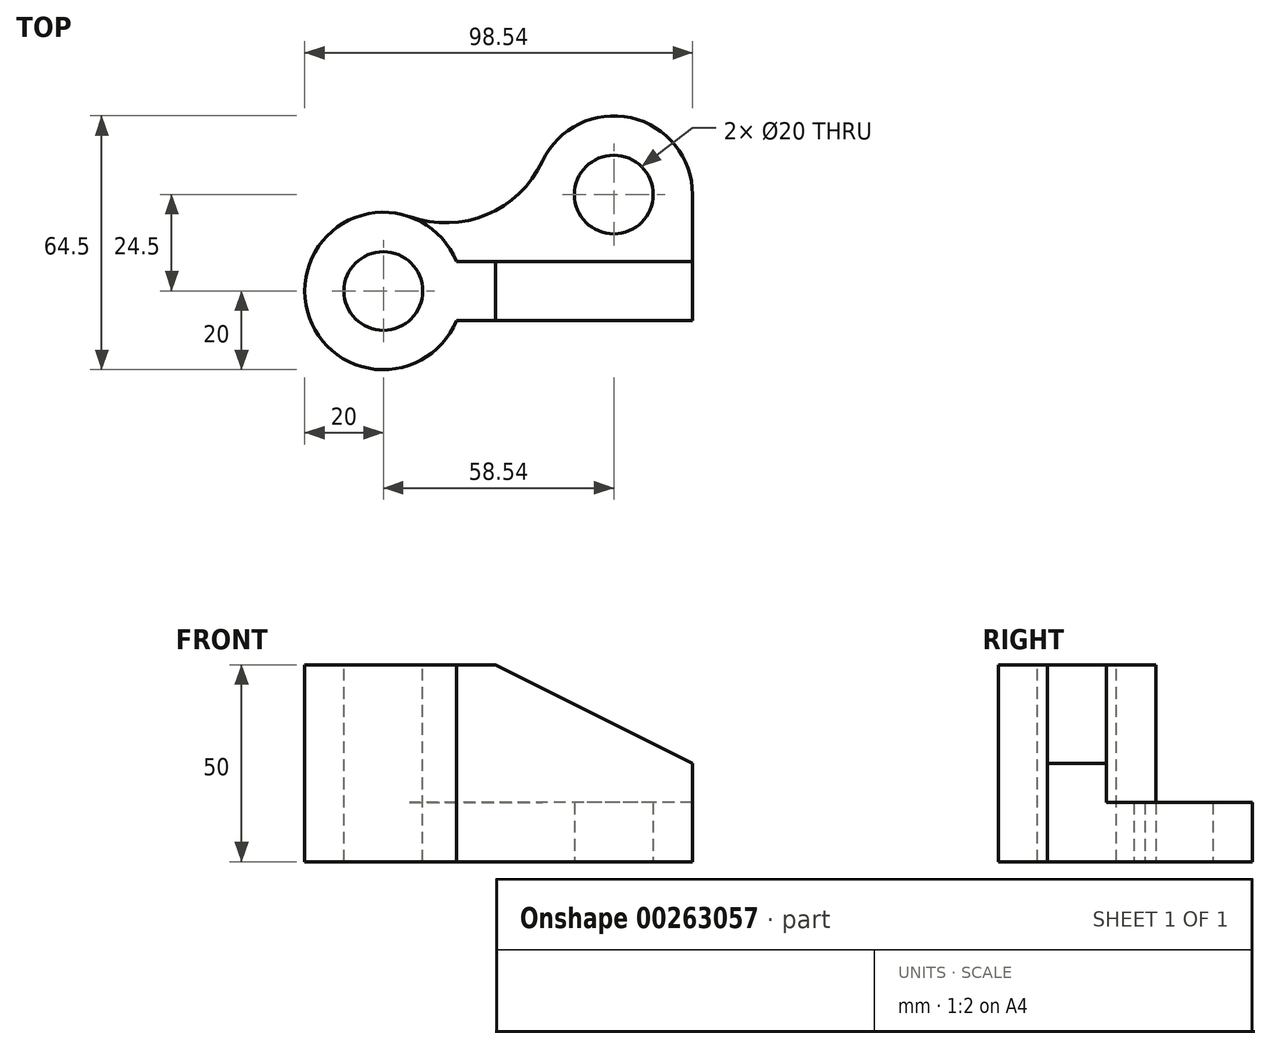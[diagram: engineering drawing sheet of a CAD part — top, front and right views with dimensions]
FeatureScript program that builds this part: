
annotation { "Feature Type Name" : "Feature", "Feature Type Description" : "" }
export const myFeature = defineFeature(function(context is Context, id is Id, definition is map)
    precondition{}
    {
        {
            var Q0;
            Q0=qCreatedBy(makeId("Top.planeOp"),FACE);
            var sketch = newSketch(context, id + "F0", { "sketchPlane" : qUnion([Q0])});
            skLineSegment(sketch, "E0", {"start": v(0, 0) * mm, "end": v(0, 32) * mm});
            skPoint(sketch, "E1", {"position": v(-78.54, 7.5) * mm});
            skLineSegment(sketch, "E2", {"start": v(0, 0) * mm, "end": v(-60, 0) * mm});
            skArc(sketch, "E3", {"start": v(0, 32) * mm, "mid": v(-15.65, 51.52) * mm, "end": v(-38.1, 40.5) * mm});
            skArc(sketch, "E4", {"start": v(-71.89, 26.36) * mm, "mid": v(-96.77, -0.72) * mm, "end": v(-60, 0) * mm});
            skArc(sketch, "E5", {"start": v(-71.89, 26.36) * mm, "mid": v(-52.27, 26.92) * mm, "end": v(-38.1, 40.5) * mm});
            skCircle(sketch, "E6", {"center": v(-20, 32) * mm, "radius": 10 * mm});
            skSolve(sketch);
        }
        {
            var Q0;
            Q0 = qSketchRegion(id + "F0", true);
            extrude(context, id + "F1", {"entities" : qUnion([Q0]), "depth" : 50 * mm});
        }
        {
            var Q0;
            Q0=makeQuery(id+"F1.opExtrude","CAP_FACE",FACE,{"disambiguationData":[OSD([sQuery(id+"F0.wireOp",EDGE,"E0"),sQuery(id+"F0.wireOp",EDGE,"E2"),sQuery(id+"F0.wireOp",EDGE,"E3"),sQuery(id+"F0.wireOp",EDGE,"E4"),sQuery(id+"F0.wireOp",EDGE,"E5"),sQuery(id+"F0.wireOp",EDGE,"E6")])],"isStart":false});
            var sketch = newSketch(context, id + "F2", { "sketchPlane" : qUnion([Q0])});
            skCircle(sketch, "E7", {"center": v(-78.54, 7.5) * mm, "radius": 10 * mm});
            skSolve(sketch);
        }
        {
            var Q0;
            Q0 = qSketchRegion(id + "F2", true);
            extrude(context, id + "F3", {"entities" : qUnion([Q0]), "operationType" : NewBodyOperationType.REMOVE, "endBound" : BoundingType.THROUGH_ALL, "oppositeDirection" : true, "depth" : 25 * mm});
        }
        {
            var Q0;
            Q0=makeQuery(id+"F1.opExtrude","CAP_FACE",FACE,{"disambiguationData":[OSD([sQuery(id+"F0.wireOp",EDGE,"E0"),sQuery(id+"F0.wireOp",EDGE,"E2"),sQuery(id+"F0.wireOp",EDGE,"E3"),sQuery(id+"F0.wireOp",EDGE,"E4"),sQuery(id+"F0.wireOp",EDGE,"E5"),sQuery(id+"F0.wireOp",EDGE,"E6")])],"isStart":false});
            var sketch = newSketch(context, id + "F4", { "sketchPlane" : qUnion([Q0])});
            skArc(sketch, "E8", {"start": v(-60, 15) * mm, "mid": v(-66.1, 23.15) * mm, "end": v(-75.41, 27.25) * mm});
            skLineSegment(sketch, "E9.bottom", {"start": v(0, 15) * mm, "end": v(-60, 15) * mm});
            skLineSegment(sketch, "E9.top", {"start": v(0, 64.45) * mm, "end": v(-75.41, 64.45) * mm});
            skLineSegment(sketch, "E9.left", {"start": v(0, 15) * mm, "end": v(0, 64.45) * mm});
            skLineSegment(sketch, "E9.right", {"start": v(-75.41, 27.25) * mm, "end": v(-75.41, 64.45) * mm});
            skSolve(sketch);
        }
        {
            var Q0;
            Q0 = qSketchRegion(id + "F4", true);
            extrude(context, id + "F5", {"entities" : qUnion([Q0]), "operationType" : NewBodyOperationType.REMOVE, "oppositeDirection" : true, "depth" : (50 - 15) * mm});
        }
        {
            var Q0;
            Q0=makeQuery(id+"F5.boolean.opBoolean","COPY",FACE,{"derivedFrom":makeQuery(id+"F5.opExtrude","SWEPT_FACE",FACE,{"disambiguationData":[OSD([sQuery(id+"F4.wireOp",EDGE,"E9.bottom")])]})});
            var sketch = newSketch(context, id + "F6", { "sketchPlane" : qUnion([Q0])});
            skLineSegment(sketch, "E10", {"start": v(0, 25) * mm, "end": v(50, 50) * mm});
            skLineSegment(sketch, "E11", {"start": v(50, 50) * mm, "end": v(0, 50) * mm});
            skLineSegment(sketch, "E12", {"start": v(0, 50) * mm, "end": v(0, 25) * mm});
            skSolve(sketch);
        }
        {
            var Q0;
            Q0 = qSketchRegion(id + "F6", true);
            extrude(context, id + "F7", {"entities" : qUnion([Q0]), "operationType" : NewBodyOperationType.REMOVE, "endBound" : BoundingType.THROUGH_ALL, "oppositeDirection" : true, "depth" : 25 * mm});
        }
    });
